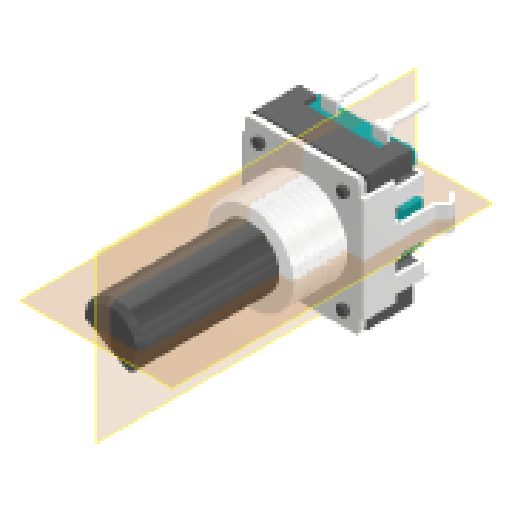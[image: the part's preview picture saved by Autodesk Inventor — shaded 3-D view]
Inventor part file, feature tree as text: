
AUTODESK INVENTOR PART (.ipt)
format: ipt  version: 2025 (Build 290162000, 162)  size: 1,793,024 bytes
history: native  units: in
note: dims shown in document units (in); Inventor stores cm internally (conversion verified against a paired STEP export)
features: imported_body x45, plane x2
ambient origin geometry x8: Origin, YZ Plane, XZ Plane, XY Plane, X Axis, Y Axis, Z Axis, Center Point
bodies: Solid1 (feature_tree), Solid2 (feature_tree), Solid3 (feature_tree), Solid4 (feature_tree), Solid5 (feature_tree), Solid6 (feature_tree), Solid7 (feature_tree), Solid8 (feature_tree), Solid9 (feature_tree), Solid10 (feature_tree), Solid11 (feature_tree), Solid12 (feature_tree), Solid13 (feature_tree), Solid14 (feature_tree), Solid15 (feature_tree), Solid16 (feature_tree), Solid17 (feature_tree), Solid18 (feature_tree), Solid19 (feature_tree), Solid20 (feature_tree), Solid21 (feature_tree), Solid22 (feature_tree), Solid23 (feature_tree), Solid24 (feature_tree), Solid25 (feature_tree), Solid26 (feature_tree), Solid27 (feature_tree), Solid28 (feature_tree), Solid29 (feature_tree), Solid30 (feature_tree), Solid31 (feature_tree), Solid32 (feature_tree), Solid33 (feature_tree), Solid34 (feature_tree), Solid35 (feature_tree), Solid36 (feature_tree), Solid37 (feature_tree), Solid38 (feature_tree), Solid39 (feature_tree), Solid40 (feature_tree), Solid41 (feature_tree), Solid42 (feature_tree), Solid43 (feature_tree), Solid44 (feature_tree), Solid45 (feature_tree)
feature tree (47):
  plane  "Work Plane1"
  plane  "Work Plane2"
  imported_body  "Base1"
  imported_body  "Base2"
  imported_body  "Base3"
  imported_body  "Base4"
  imported_body  "Base5"
  imported_body  "Base6"
  imported_body  "Base7"
  imported_body  "Base8"
  imported_body  "Base9"
  imported_body  "Base10"
  imported_body  "Base11"
  imported_body  "Base12"
  imported_body  "Base13"
  imported_body  "Base14"
  imported_body  "Base15"
  imported_body  "Base16"
  imported_body  "Base17"
  imported_body  "Base18"
  imported_body  "Base19"
  imported_body  "Base20"
  imported_body  "Base21"
  imported_body  "Base22"
  imported_body  "Base23"
  imported_body  "Base24"
  imported_body  "Base25"
  imported_body  "Base26"
  imported_body  "Base27"
  imported_body  "Base28"
  imported_body  "Base29"
  imported_body  "Base30"
  imported_body  "Base31"
  imported_body  "Base32"
  imported_body  "Base33"
  imported_body  "Base34"
  imported_body  "Base35"
  imported_body  "Base36"
  imported_body  "Base37"
  imported_body  "Base38"
  imported_body  "Base39"
  imported_body  "Base40"
  imported_body  "Base41"
  imported_body  "Base42"
  imported_body  "Base43"
  imported_body  "Base44"
  imported_body  "Base45"
